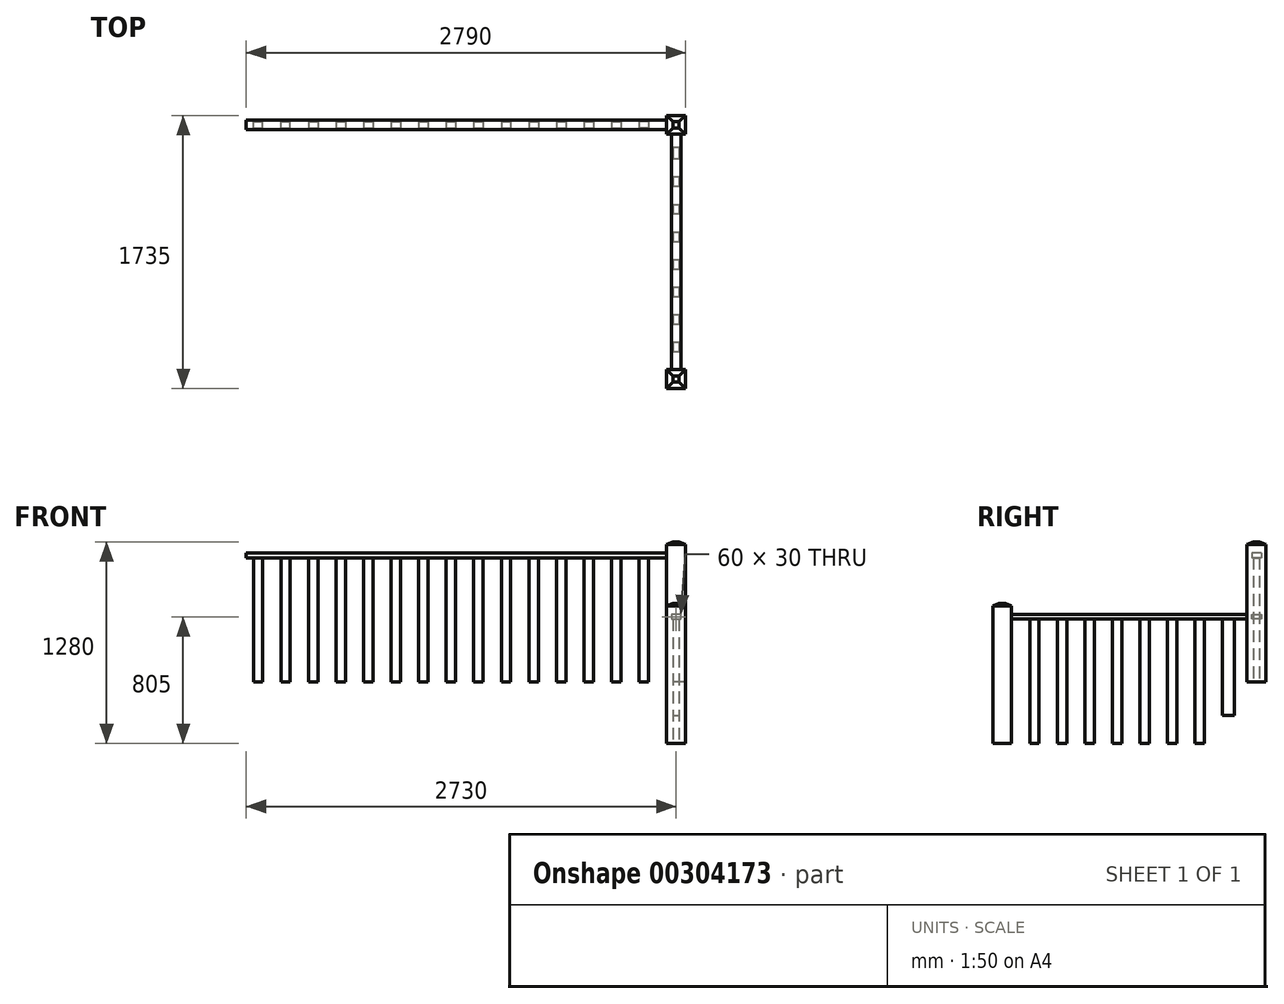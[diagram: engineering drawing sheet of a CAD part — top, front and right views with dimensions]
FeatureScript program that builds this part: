
annotation { "Feature Type Name" : "Feature", "Feature Type Description" : "" }
export const myFeature = defineFeature(function(context is Context, id is Id, definition is map)
    precondition{}
    {
        {
            var Q0;
            Q0=qCreatedBy(makeId("Top.planeOp"),FACE);
            var sketch = newSketch(context, id + "F0", { "sketchPlane" : qUnion([Q0])});
            skLineSegment(sketch, "E0.bottom", {"start": v(-80, 328.24) * mm, "end": v(40, 328.24) * mm});
            skLineSegment(sketch, "E0.top", {"start": v(-80, 208.24) * mm, "end": v(40, 208.24) * mm});
            skLineSegment(sketch, "E0.left", {"start": v(-80, 328.24) * mm, "end": v(-80, 208.24) * mm});
            skLineSegment(sketch, "E0.right", {"start": v(40, 328.24) * mm, "end": v(40, 208.24) * mm});
            skLineSegment(sketch, "E1.top", {"start": v(-80, 1823.24) * mm, "end": v(40, 1823.24) * mm});
            skLineSegment(sketch, "E1.left", {"start": v(-80, 1943.24) * mm, "end": v(-80, 1823.24) * mm});
            skLineSegment(sketch, "E1.right", {"start": v(40, 1943.24) * mm, "end": v(40, 1823.24) * mm});
            skLineSegment(sketch, "E2.bottom", {"start": v(-40, 503.24) * mm, "end": v(0, 503.24) * mm});
            skLineSegment(sketch, "E2.top", {"start": v(-40, 443.24) * mm, "end": v(0, 443.24) * mm});
            skLineSegment(sketch, "E2.left", {"start": v(-40, 503.24) * mm, "end": v(-40, 443.24) * mm});
            skLineSegment(sketch, "E2.right", {"start": v(0, 503.24) * mm, "end": v(0, 443.24) * mm});
            skLineSegment(sketch, "E3.bottom", {"start": v(-40, 678.24) * mm, "end": v(0, 678.24) * mm});
            skLineSegment(sketch, "E3.top", {"start": v(-40, 618.24) * mm, "end": v(0, 618.24) * mm});
            skLineSegment(sketch, "E3.left", {"start": v(-40, 678.24) * mm, "end": v(-40, 618.24) * mm});
            skLineSegment(sketch, "E3.right", {"start": v(0, 678.24) * mm, "end": v(0, 618.24) * mm});
            skLineSegment(sketch, "E4.bottom", {"start": v(-40, 853.24) * mm, "end": v(0, 853.24) * mm});
            skLineSegment(sketch, "E4.top", {"start": v(-40, 793.24) * mm, "end": v(0, 793.24) * mm});
            skLineSegment(sketch, "E4.left", {"start": v(-40, 853.24) * mm, "end": v(-40, 793.24) * mm});
            skLineSegment(sketch, "E4.right", {"start": v(0, 853.24) * mm, "end": v(0, 793.24) * mm});
            skLineSegment(sketch, "E5.bottom", {"start": v(-40, 1028.24) * mm, "end": v(0, 1028.24) * mm});
            skLineSegment(sketch, "E5.top", {"start": v(-40, 968.24) * mm, "end": v(0, 968.24) * mm});
            skLineSegment(sketch, "E5.left", {"start": v(-40, 1028.24) * mm, "end": v(-40, 968.24) * mm});
            skLineSegment(sketch, "E5.right", {"start": v(0, 1028.24) * mm, "end": v(0, 968.24) * mm});
            skLineSegment(sketch, "E6.bottom", {"start": v(-40, 1203.24) * mm, "end": v(0, 1203.24) * mm});
            skLineSegment(sketch, "E6.top", {"start": v(-40, 1143.24) * mm, "end": v(0, 1143.24) * mm});
            skLineSegment(sketch, "E6.left", {"start": v(-40, 1203.24) * mm, "end": v(-40, 1143.24) * mm});
            skLineSegment(sketch, "E6.right", {"start": v(0, 1203.24) * mm, "end": v(0, 1143.24) * mm});
            skLineSegment(sketch, "E7.bottom", {"start": v(-40, 1378.24) * mm, "end": v(0, 1378.24) * mm});
            skLineSegment(sketch, "E7.top", {"start": v(-40, 1318.24) * mm, "end": v(0, 1318.24) * mm});
            skLineSegment(sketch, "E7.left", {"start": v(-40, 1378.24) * mm, "end": v(-40, 1318.24) * mm});
            skLineSegment(sketch, "E7.right", {"start": v(0, 1378.24) * mm, "end": v(0, 1318.24) * mm});
            skLineSegment(sketch, "E8.bottom", {"start": v(-40, 1553.24) * mm, "end": v(0, 1553.24) * mm});
            skLineSegment(sketch, "E8.top", {"start": v(-40, 1493.24) * mm, "end": v(0, 1493.24) * mm});
            skLineSegment(sketch, "E8.left", {"start": v(-40, 1553.24) * mm, "end": v(-40, 1493.24) * mm});
            skLineSegment(sketch, "E8.right", {"start": v(0, 1553.24) * mm, "end": v(0, 1478.21) * mm});
            skLineSegment(sketch, "E9.bottom", {"start": v(-40, 1743.26) * mm, "end": v(0, 1743.26) * mm});
            skLineSegment(sketch, "E9.top", {"start": v(-40, 1668.24) * mm, "end": v(0, 1668.24) * mm});
            skLineSegment(sketch, "E9.left", {"start": v(-40, 1743.26) * mm, "end": v(-40, 1668.24) * mm});
            skLineSegment(sketch, "E9.right", {"start": v(0, 1743.26) * mm, "end": v(0, 1668.24) * mm});
            skLineSegment(sketch, "E10", {"start": v(40, 1943.24) * mm, "end": v(-80, 1943.24) * mm});
            skLineSegment(sketch, "E11.bottom", {"start": v(-195, 1903.24) * mm, "end": v(-255, 1903.24) * mm});
            skLineSegment(sketch, "E11.top", {"start": v(-195, 1863.24) * mm, "end": v(-255, 1863.24) * mm});
            skLineSegment(sketch, "E11.left", {"start": v(-195, 1903.24) * mm, "end": v(-195, 1863.24) * mm});
            skLineSegment(sketch, "E11.right", {"start": v(-255, 1903.24) * mm, "end": v(-255, 1863.24) * mm});
            skLineSegment(sketch, "E12.bottom", {"start": v(-370, 1903.24) * mm, "end": v(-430, 1903.24) * mm});
            skLineSegment(sketch, "E12.top", {"start": v(-370, 1863.24) * mm, "end": v(-430, 1863.24) * mm});
            skLineSegment(sketch, "E12.left", {"start": v(-370, 1903.24) * mm, "end": v(-370, 1863.24) * mm});
            skLineSegment(sketch, "E12.right", {"start": v(-430, 1903.24) * mm, "end": v(-430, 1863.24) * mm});
            skLineSegment(sketch, "E13.bottom", {"start": v(-545, 1903.24) * mm, "end": v(-605, 1903.24) * mm});
            skLineSegment(sketch, "E13.top", {"start": v(-545, 1863.24) * mm, "end": v(-605, 1863.24) * mm});
            skLineSegment(sketch, "E13.left", {"start": v(-545, 1903.24) * mm, "end": v(-545, 1863.24) * mm});
            skLineSegment(sketch, "E13.right", {"start": v(-605, 1903.24) * mm, "end": v(-605, 1863.24) * mm});
            skLineSegment(sketch, "E14.bottom", {"start": v(-720, 1903.24) * mm, "end": v(-780, 1903.24) * mm});
            skLineSegment(sketch, "E14.top", {"start": v(-720, 1863.24) * mm, "end": v(-780, 1863.24) * mm});
            skLineSegment(sketch, "E14.left", {"start": v(-720, 1903.24) * mm, "end": v(-720, 1863.24) * mm});
            skLineSegment(sketch, "E14.right", {"start": v(-780, 1903.24) * mm, "end": v(-780, 1863.24) * mm});
            skLineSegment(sketch, "E15.bottom", {"start": v(-895, 1903.24) * mm, "end": v(-955, 1903.24) * mm});
            skLineSegment(sketch, "E15.top", {"start": v(-895, 1863.24) * mm, "end": v(-955, 1863.24) * mm});
            skLineSegment(sketch, "E15.left", {"start": v(-895, 1903.24) * mm, "end": v(-895, 1863.24) * mm});
            skLineSegment(sketch, "E15.right", {"start": v(-955, 1903.24) * mm, "end": v(-955, 1863.24) * mm});
            skLineSegment(sketch, "E16.bottom", {"start": v(-1070, 1903.24) * mm, "end": v(-1130, 1903.24) * mm});
            skLineSegment(sketch, "E16.top", {"start": v(-1070, 1863.24) * mm, "end": v(-1130, 1863.24) * mm});
            skLineSegment(sketch, "E16.left", {"start": v(-1070, 1903.24) * mm, "end": v(-1070, 1863.24) * mm});
            skLineSegment(sketch, "E16.right", {"start": v(-1130, 1903.24) * mm, "end": v(-1130, 1863.24) * mm});
            skLineSegment(sketch, "E17.bottom", {"start": v(-1245, 1903.24) * mm, "end": v(-1305, 1903.24) * mm});
            skLineSegment(sketch, "E17.top", {"start": v(-1245, 1863.24) * mm, "end": v(-1305, 1863.24) * mm});
            skLineSegment(sketch, "E17.left", {"start": v(-1245, 1903.24) * mm, "end": v(-1245, 1863.24) * mm});
            skLineSegment(sketch, "E17.right", {"start": v(-1305, 1903.24) * mm, "end": v(-1305, 1863.24) * mm});
            skLineSegment(sketch, "E18.bottom", {"start": v(-1420, 1903.24) * mm, "end": v(-1480, 1903.24) * mm});
            skLineSegment(sketch, "E18.top", {"start": v(-1420, 1863.24) * mm, "end": v(-1480, 1863.24) * mm});
            skLineSegment(sketch, "E18.left", {"start": v(-1420, 1903.24) * mm, "end": v(-1420, 1863.24) * mm});
            skLineSegment(sketch, "E18.right", {"start": v(-1480, 1903.24) * mm, "end": v(-1480, 1863.24) * mm});
            skLineSegment(sketch, "E19.bottom", {"start": v(-1655, 1903.24) * mm, "end": v(-1595, 1903.24) * mm});
            skLineSegment(sketch, "E19.top", {"start": v(-1655, 1863.24) * mm, "end": v(-1595, 1863.24) * mm});
            skLineSegment(sketch, "E19.left", {"start": v(-1655, 1903.24) * mm, "end": v(-1655, 1863.24) * mm});
            skLineSegment(sketch, "E19.right", {"start": v(-1595, 1903.24) * mm, "end": v(-1595, 1863.24) * mm});
            skLineSegment(sketch, "E20.bottom", {"start": v(-1830, 1903.24) * mm, "end": v(-1770, 1903.24) * mm});
            skLineSegment(sketch, "E20.top", {"start": v(-1830, 1863.24) * mm, "end": v(-1770, 1863.24) * mm});
            skLineSegment(sketch, "E20.left", {"start": v(-1830, 1903.24) * mm, "end": v(-1830, 1863.24) * mm});
            skLineSegment(sketch, "E20.right", {"start": v(-1770, 1903.24) * mm, "end": v(-1770, 1863.24) * mm});
            skLineSegment(sketch, "E21.bottom", {"start": v(-2005, 1903.24) * mm, "end": v(-1945, 1903.24) * mm});
            skLineSegment(sketch, "E21.top", {"start": v(-2005, 1863.24) * mm, "end": v(-1945, 1863.24) * mm});
            skLineSegment(sketch, "E21.left", {"start": v(-2005, 1903.24) * mm, "end": v(-2005, 1863.24) * mm});
            skLineSegment(sketch, "E21.right", {"start": v(-1945, 1903.24) * mm, "end": v(-1945, 1863.24) * mm});
            skLineSegment(sketch, "E22.bottom", {"start": v(-2180, 1903.24) * mm, "end": v(-2120, 1903.24) * mm});
            skLineSegment(sketch, "E22.top", {"start": v(-2180, 1863.24) * mm, "end": v(-2120, 1863.24) * mm});
            skLineSegment(sketch, "E22.left", {"start": v(-2180, 1903.24) * mm, "end": v(-2180, 1863.24) * mm});
            skLineSegment(sketch, "E22.right", {"start": v(-2120, 1903.24) * mm, "end": v(-2120, 1863.24) * mm});
            skLineSegment(sketch, "E23.bottom", {"start": v(-2355, 1903.24) * mm, "end": v(-2295, 1903.24) * mm});
            skLineSegment(sketch, "E23.top", {"start": v(-2355, 1863.24) * mm, "end": v(-2295, 1863.24) * mm});
            skLineSegment(sketch, "E23.left", {"start": v(-2355, 1903.24) * mm, "end": v(-2355, 1863.24) * mm});
            skLineSegment(sketch, "E23.right", {"start": v(-2295, 1903.24) * mm, "end": v(-2295, 1863.24) * mm});
            skSolve(sketch);
        }
        {
            var Q0;
            Q0=makeQuery(id+"F0.imprint","IMPRINT",FACE,{"disambiguationData":[TD([[makeQuery(id+"F0.imprint","IMPRINT",EDGE,{"derivedFrom":sQuery(id+"F0.wireOp",EDGE,"E23.bottom")}),-1.0]])]});
            var Q1;
            Q1=makeQuery(id+"F0.imprint","IMPRINT",FACE,{"disambiguationData":[TD([[makeQuery(id+"F0.imprint","IMPRINT",EDGE,{"derivedFrom":sQuery(id+"F0.wireOp",EDGE,"E22.bottom")}),-1.0]])]});
            var Q2;
            Q2=makeQuery(id+"F0.imprint","IMPRINT",FACE,{"disambiguationData":[TD([[makeQuery(id+"F0.imprint","IMPRINT",EDGE,{"derivedFrom":sQuery(id+"F0.wireOp",EDGE,"E21.bottom")}),-1.0]])]});
            var Q3;
            Q3=makeQuery(id+"F0.imprint","IMPRINT",FACE,{"disambiguationData":[TD([[makeQuery(id+"F0.imprint","IMPRINT",EDGE,{"derivedFrom":sQuery(id+"F0.wireOp",EDGE,"E20.bottom")}),-1.0]])]});
            var Q4;
            Q4=makeQuery(id+"F0.imprint","IMPRINT",FACE,{"disambiguationData":[TD([[makeQuery(id+"F0.imprint","IMPRINT",EDGE,{"derivedFrom":sQuery(id+"F0.wireOp",EDGE,"E19.bottom")}),-1.0]])]});
            var Q5;
            Q5=makeQuery(id+"F0.imprint","IMPRINT",FACE,{"disambiguationData":[TD([[makeQuery(id+"F0.imprint","IMPRINT",EDGE,{"derivedFrom":sQuery(id+"F0.wireOp",EDGE,"E18.bottom")}),1.0]])]});
            var Q6;
            Q6=makeQuery(id+"F0.imprint","IMPRINT",FACE,{"disambiguationData":[TD([[makeQuery(id+"F0.imprint","IMPRINT",EDGE,{"derivedFrom":sQuery(id+"F0.wireOp",EDGE,"E17.bottom")}),1.0]])]});
            var Q7;
            Q7=makeQuery(id+"F0.imprint","IMPRINT",FACE,{"disambiguationData":[TD([[makeQuery(id+"F0.imprint","IMPRINT",EDGE,{"derivedFrom":sQuery(id+"F0.wireOp",EDGE,"E16.bottom")}),1.0]])]});
            var Q8;
            Q8=makeQuery(id+"F0.imprint","IMPRINT",FACE,{"disambiguationData":[TD([[makeQuery(id+"F0.imprint","IMPRINT",EDGE,{"derivedFrom":sQuery(id+"F0.wireOp",EDGE,"E15.bottom")}),1.0]])]});
            var Q9;
            Q9=makeQuery(id+"F0.imprint","IMPRINT",FACE,{"disambiguationData":[TD([[makeQuery(id+"F0.imprint","IMPRINT",EDGE,{"derivedFrom":sQuery(id+"F0.wireOp",EDGE,"E14.bottom")}),1.0]])]});
            var Q10;
            Q10=makeQuery(id+"F0.imprint","IMPRINT",FACE,{"disambiguationData":[TD([[makeQuery(id+"F0.imprint","IMPRINT",EDGE,{"derivedFrom":sQuery(id+"F0.wireOp",EDGE,"E13.bottom")}),1.0]])]});
            var Q11;
            Q11=makeQuery(id+"F0.imprint","IMPRINT",FACE,{"disambiguationData":[TD([[makeQuery(id+"F0.imprint","IMPRINT",EDGE,{"derivedFrom":sQuery(id+"F0.wireOp",EDGE,"E12.bottom")}),1.0]])]});
            var Q12;
            Q12=makeQuery(id+"F0.imprint","IMPRINT",FACE,{"disambiguationData":[TD([[makeQuery(id+"F0.imprint","IMPRINT",EDGE,{"derivedFrom":sQuery(id+"F0.wireOp",EDGE,"E11.bottom")}),1.0]])]});
            var Q13;
            Q13=makeQuery(id+"F0.imprint","IMPRINT",FACE,{"disambiguationData":[TD([[makeQuery(id+"F0.imprint","IMPRINT",EDGE,{"derivedFrom":sQuery(id+"F0.wireOp",EDGE,"E9.bottom")}),-1.0]])]});
            var Q14;
            {var subQ0=sQuery(id+"F0.wireOp",EDGE,"E8.bottom");Q14=makeQuery(id+"F0.imprint","IMPRINT",FACE,{"disambiguationData":[TD([[makeQuery(id+"F0.imprint","IMPRINT",EDGE,{"derivedFrom":subQ0}),-1.0]])]});}
            var Q15;
            Q15=makeQuery(id+"F0.imprint","IMPRINT",FACE,{"disambiguationData":[TD([[makeQuery(id+"F0.imprint","IMPRINT",EDGE,{"derivedFrom":sQuery(id+"F0.wireOp",EDGE,"E7.bottom")}),-1.0]])]});
            var Q16;
            Q16=makeQuery(id+"F0.imprint","IMPRINT",FACE,{"disambiguationData":[TD([[makeQuery(id+"F0.imprint","IMPRINT",EDGE,{"derivedFrom":sQuery(id+"F0.wireOp",EDGE,"E6.bottom")}),-1.0]])]});
            var Q17;
            Q17=makeQuery(id+"F0.imprint","IMPRINT",FACE,{"disambiguationData":[TD([[makeQuery(id+"F0.imprint","IMPRINT",EDGE,{"derivedFrom":sQuery(id+"F0.wireOp",EDGE,"E5.bottom")}),-1.0]])]});
            var Q18;
            Q18=makeQuery(id+"F0.imprint","IMPRINT",FACE,{"disambiguationData":[TD([[makeQuery(id+"F0.imprint","IMPRINT",EDGE,{"derivedFrom":sQuery(id+"F0.wireOp",EDGE,"E4.bottom")}),-1.0]])]});
            var Q19;
            Q19=makeQuery(id+"F0.imprint","IMPRINT",FACE,{"disambiguationData":[TD([[makeQuery(id+"F0.imprint","IMPRINT",EDGE,{"derivedFrom":sQuery(id+"F0.wireOp",EDGE,"E3.bottom")}),-1.0]])]});
            var Q20;
            Q20=makeQuery(id+"F0.imprint","IMPRINT",FACE,{"disambiguationData":[TD([[makeQuery(id+"F0.imprint","IMPRINT",EDGE,{"derivedFrom":sQuery(id+"F0.wireOp",EDGE,"E2.bottom")}),-1.0]])]});
            var Q21;
            Q21=makeQuery(id+"F0.imprint","IMPRINT",FACE,{"disambiguationData":[TD([[makeQuery(id+"F0.imprint","IMPRINT",EDGE,{"derivedFrom":sQuery(id+"F0.wireOp",EDGE,"E1.top")}),1.0]])]});
            var Q22;
            Q22=makeQuery(id+"F0.imprint","IMPRINT",FACE,{"disambiguationData":[TD([[makeQuery(id+"F0.imprint","IMPRINT",EDGE,{"derivedFrom":sQuery(id+"F0.wireOp",EDGE,"E0.bottom")}),-1.0]])]});
            extrude(context, id + "F1", {"entities" : qUnion([Q0, Q1, Q2, Q3, Q4, Q5, Q6, Q7, Q8, Q9, Q10, Q11, Q12, Q13, Q14, Q15, Q16, Q17, Q18, Q19, Q20, Q21, Q22]), "depth" : 790 * mm});
        }
        {
            var Q0;
            Q0=makeQuery(id+"F1.opExtrude","CAP_FACE",FACE,{"disambiguationData":[OSD([sQuery(id+"F0.wireOp",EDGE,"E9.bottom"),sQuery(id+"F0.wireOp",EDGE,"E9.top"),sQuery(id+"F0.wireOp",EDGE,"E9.left"),sQuery(id+"F0.wireOp",EDGE,"E9.right")])],"isStart":false});
            var sketch = newSketch(context, id + "F2", { "sketchPlane" : qUnion([Q0])});
            skPoint(sketch, "E24.0", {"position": v(-20, 328.24) * mm});
            skLineSegment(sketch, "E25.0", {"start": v(-80, 328.24) * mm, "end": v(40, 328.24) * mm});
            skLineSegment(sketch, "E26.0.0", {"start": v(-80, 328.24) * mm, "end": v(-80, 208.24) * mm});
            skLineSegment(sketch, "E26.0.1", {"start": v(-80, 208.24) * mm, "end": v(40, 208.24) * mm});
            skLineSegment(sketch, "E26.0.2", {"start": v(40, 208.24) * mm, "end": v(40, 328.24) * mm});
            skLineSegment(sketch, "E26.0.3", {"start": v(40, 328.24) * mm, "end": v(-80, 328.24) * mm});
            skLineSegment(sketch, "E27", {"start": v(-50, 1853.24) * mm, "end": v(-2417.72, 1853.24) * mm});
            skLineSegment(sketch, "E28", {"start": v(-2417.72, 1853.24) * mm, "end": v(-2417.72, 1913.24) * mm});
            skLineSegment(sketch, "E29", {"start": v(-2417.72, 1913.24) * mm, "end": v(10, 1913.24) * mm});
            skLineSegment(sketch, "E30", {"start": v(10, 1913.24) * mm, "end": v(10, 328.24) * mm});
            skLineSegment(sketch, "E31", {"start": v(10, 328.24) * mm, "end": v(-50, 328.24) * mm});
            skLineSegment(sketch, "E32", {"start": v(-50, 328.24) * mm, "end": v(-50, 1853.24) * mm});
            skSolve(sketch);
        }
        {
            var Q0;
            Q0 = qSketchRegion(id + "F2", true);
            extrude(context, id + "F3", {"entities" : qUnion([Q0]), "depth" : 30 * mm});
        }
        {
            var Q0;
            Q0=makeQuery(id+"F1.opExtrude","CAP_FACE",FACE,{"disambiguationData":[OSD([sQuery(id+"F0.wireOp",EDGE,"E1.top"),sQuery(id+"F0.wireOp",EDGE,"E1.left"),sQuery(id+"F0.wireOp",EDGE,"E1.right"),sQuery(id+"F0.wireOp",EDGE,"E10")])],"isStart":false});
            var sketch = newSketch(context, id + "F4", { "sketchPlane" : qUnion([Q0])});
            skLineSegment(sketch, "E33.0", {"start": v(40, 1943.24) * mm, "end": v(-80, 1943.24) * mm});
            skLineSegment(sketch, "E34.0", {"start": v(-80, 1943.24) * mm, "end": v(-80, 1823.24) * mm});
            skLineSegment(sketch, "E35.0", {"start": v(-80, 1823.24) * mm, "end": v(40, 1823.24) * mm});
            skLineSegment(sketch, "E36.0", {"start": v(40, 1943.24) * mm, "end": v(40, 1823.24) * mm});
            skLineSegment(sketch, "E37.0", {"start": v(-80, 328.24) * mm, "end": v(-80, 208.24) * mm});
            skPoint(sketch, "E38.0", {"position": v(40, 208.24) * mm});
            skLineSegment(sketch, "E39.bottom", {"start": v(-80, 328.24) * mm, "end": v(40, 328.24) * mm});
            skLineSegment(sketch, "E39.top", {"start": v(-80, 208.24) * mm, "end": v(40, 208.24) * mm});
            skLineSegment(sketch, "E39.right", {"start": v(40, 328.24) * mm, "end": v(40, 208.24) * mm});
            skLineSegment(sketch, "E40.bottom", {"start": v(-80, 1943.24) * mm, "end": v(40, 1943.24) * mm});
            skSolve(sketch);
        }
        {
            var Q0;
            Q0 = qSketchRegion(id + "F4", true);
            extrude(context, id + "F5", {"entities" : qUnion([Q0]), "depth" : 100 * mm});
        }
        {
            var Q0;
            Q0=makeQuery(id+"F5.opExtrude","CAP_EDGE",EDGE,{"disambiguationData":[OSD([sQuery(id+"F4.wireOp",EDGE,"E39.right")])],"isStart":false});
            var Q1;
            Q1=makeQuery(id+"F5.opExtrude","CAP_EDGE",EDGE,{"disambiguationData":[OSD([sQuery(id+"F4.wireOp",EDGE,"E39.top")])],"isStart":false});
            var Q2;
            Q2=makeQuery(id+"F5.opExtrude","CAP_EDGE",EDGE,{"disambiguationData":[OSD([sQuery(id+"F4.wireOp",EDGE,"E37.0")])],"isStart":false});
            var Q3;
            Q3=makeQuery(id+"F5.opExtrude","CAP_EDGE",EDGE,{"disambiguationData":[OSD([sQuery(id+"F4.wireOp",EDGE,"E39.bottom")])],"isStart":false});
            chamfer(context, id + "F6", {"entities" : qUnion([Q0, Q1, Q2, Q3]), "chamferType" : ChamferType.TWO_OFFSETS, "width1" : 15 * mm, "oppositeDirection" : false, "width2" : 40 * mm, "tangentPropagation" : true});
        }
        {
            var Q0;
            Q0=makeQuery(id+"F1.opExtrude","SWEPT_BODY",BODY,{"disambiguationData":[OSD([sQuery(id+"F0.wireOp",EDGE,"E0.bottom"),sQuery(id+"F0.wireOp",EDGE,"E0.top"),sQuery(id+"F0.wireOp",EDGE,"E0.left"),sQuery(id+"F0.wireOp",EDGE,"E0.right")])]});
            var Q1;
            Q1=makeQuery(id+"F1.opExtrude","SWEPT_BODY",BODY,{"disambiguationData":[OSD([sQuery(id+"F0.wireOp",EDGE,"E1.top"),sQuery(id+"F0.wireOp",EDGE,"E1.left"),sQuery(id+"F0.wireOp",EDGE,"E1.right"),sQuery(id+"F0.wireOp",EDGE,"E10")])]});
            var Q2;
            Q2=makeQuery(id+"F1.opExtrude","SWEPT_BODY",BODY,{"disambiguationData":[OSD([sQuery(id+"F0.wireOp",EDGE,"E2.bottom"),sQuery(id+"F0.wireOp",EDGE,"E2.top"),sQuery(id+"F0.wireOp",EDGE,"E2.left"),sQuery(id+"F0.wireOp",EDGE,"E2.right")])]});
            var Q3;
            Q3=makeQuery(id+"F1.opExtrude","SWEPT_BODY",BODY,{"disambiguationData":[OSD([sQuery(id+"F0.wireOp",EDGE,"E3.bottom"),sQuery(id+"F0.wireOp",EDGE,"E3.top"),sQuery(id+"F0.wireOp",EDGE,"E3.left"),sQuery(id+"F0.wireOp",EDGE,"E3.right")])]});
            var Q4;
            Q4=makeQuery(id+"F1.opExtrude","SWEPT_BODY",BODY,{"disambiguationData":[OSD([sQuery(id+"F0.wireOp",EDGE,"E4.bottom"),sQuery(id+"F0.wireOp",EDGE,"E4.top"),sQuery(id+"F0.wireOp",EDGE,"E4.left"),sQuery(id+"F0.wireOp",EDGE,"E4.right")])]});
            var Q5;
            Q5=makeQuery(id+"F1.opExtrude","SWEPT_BODY",BODY,{"disambiguationData":[OSD([sQuery(id+"F0.wireOp",EDGE,"E5.bottom"),sQuery(id+"F0.wireOp",EDGE,"E5.top"),sQuery(id+"F0.wireOp",EDGE,"E5.left"),sQuery(id+"F0.wireOp",EDGE,"E5.right")])]});
            var Q6;
            Q6=makeQuery(id+"F1.opExtrude","SWEPT_BODY",BODY,{"disambiguationData":[OSD([sQuery(id+"F0.wireOp",EDGE,"E6.bottom"),sQuery(id+"F0.wireOp",EDGE,"E6.top"),sQuery(id+"F0.wireOp",EDGE,"E6.left"),sQuery(id+"F0.wireOp",EDGE,"E6.right")])]});
            var Q7;
            Q7=makeQuery(id+"F1.opExtrude","SWEPT_BODY",BODY,{"disambiguationData":[OSD([sQuery(id+"F0.wireOp",EDGE,"E7.bottom"),sQuery(id+"F0.wireOp",EDGE,"E7.top"),sQuery(id+"F0.wireOp",EDGE,"E7.left"),sQuery(id+"F0.wireOp",EDGE,"E7.right")])]});
            var Q8;
            Q8=makeQuery(id+"F1.opExtrude","SWEPT_BODY",BODY,{"disambiguationData":[OSD([sQuery(id+"F0.wireOp",EDGE,"E8.bottom"),sQuery(id+"F0.wireOp",EDGE,"E8.top"),sQuery(id+"F0.wireOp",EDGE,"E8.left"),sQuery(id+"F0.wireOp",EDGE,"E8.right")])]});
            var Q9;
            Q9=makeQuery(id+"F1.opExtrude","SWEPT_BODY",BODY,{"disambiguationData":[OSD([sQuery(id+"F0.wireOp",EDGE,"E9.bottom"),sQuery(id+"F0.wireOp",EDGE,"E9.top"),sQuery(id+"F0.wireOp",EDGE,"E9.left"),sQuery(id+"F0.wireOp",EDGE,"E9.right")])]});
            var Q10;
            Q10=makeQuery(id+"F1.opExtrude","SWEPT_BODY",BODY,{"disambiguationData":[OSD([sQuery(id+"F0.wireOp",EDGE,"E11.bottom"),sQuery(id+"F0.wireOp",EDGE,"E11.top"),sQuery(id+"F0.wireOp",EDGE,"E11.left"),sQuery(id+"F0.wireOp",EDGE,"E11.right")])]});
            var Q11;
            Q11=makeQuery(id+"F1.opExtrude","SWEPT_BODY",BODY,{"disambiguationData":[OSD([sQuery(id+"F0.wireOp",EDGE,"E12.bottom"),sQuery(id+"F0.wireOp",EDGE,"E12.top"),sQuery(id+"F0.wireOp",EDGE,"E12.left"),sQuery(id+"F0.wireOp",EDGE,"E12.right")])]});
            var Q12;
            Q12=makeQuery(id+"F1.opExtrude","SWEPT_BODY",BODY,{"disambiguationData":[OSD([sQuery(id+"F0.wireOp",EDGE,"E13.bottom"),sQuery(id+"F0.wireOp",EDGE,"E13.top"),sQuery(id+"F0.wireOp",EDGE,"E13.left"),sQuery(id+"F0.wireOp",EDGE,"E13.right")])]});
            var Q13;
            Q13=makeQuery(id+"F1.opExtrude","SWEPT_BODY",BODY,{"disambiguationData":[OSD([sQuery(id+"F0.wireOp",EDGE,"E14.bottom"),sQuery(id+"F0.wireOp",EDGE,"E14.top"),sQuery(id+"F0.wireOp",EDGE,"E14.left"),sQuery(id+"F0.wireOp",EDGE,"E14.right")])]});
            var Q14;
            Q14=makeQuery(id+"F1.opExtrude","SWEPT_BODY",BODY,{"disambiguationData":[OSD([sQuery(id+"F0.wireOp",EDGE,"E15.bottom"),sQuery(id+"F0.wireOp",EDGE,"E15.top"),sQuery(id+"F0.wireOp",EDGE,"E15.left"),sQuery(id+"F0.wireOp",EDGE,"E15.right")])]});
            var Q15;
            Q15=makeQuery(id+"F1.opExtrude","SWEPT_BODY",BODY,{"disambiguationData":[OSD([sQuery(id+"F0.wireOp",EDGE,"E16.bottom"),sQuery(id+"F0.wireOp",EDGE,"E16.top"),sQuery(id+"F0.wireOp",EDGE,"E16.left"),sQuery(id+"F0.wireOp",EDGE,"E16.right")])]});
            var Q16;
            Q16=makeQuery(id+"F1.opExtrude","SWEPT_BODY",BODY,{"disambiguationData":[OSD([sQuery(id+"F0.wireOp",EDGE,"E17.bottom"),sQuery(id+"F0.wireOp",EDGE,"E17.top"),sQuery(id+"F0.wireOp",EDGE,"E17.left"),sQuery(id+"F0.wireOp",EDGE,"E17.right")])]});
            var Q17;
            Q17=makeQuery(id+"F1.opExtrude","SWEPT_BODY",BODY,{"disambiguationData":[OSD([sQuery(id+"F0.wireOp",EDGE,"E18.bottom"),sQuery(id+"F0.wireOp",EDGE,"E18.top"),sQuery(id+"F0.wireOp",EDGE,"E18.left"),sQuery(id+"F0.wireOp",EDGE,"E18.right")])]});
            var Q18;
            Q18=makeQuery(id+"F1.opExtrude","SWEPT_BODY",BODY,{"disambiguationData":[OSD([sQuery(id+"F0.wireOp",EDGE,"E19.bottom"),sQuery(id+"F0.wireOp",EDGE,"E19.top"),sQuery(id+"F0.wireOp",EDGE,"E19.left"),sQuery(id+"F0.wireOp",EDGE,"E19.right")])]});
            var Q19;
            Q19=makeQuery(id+"F1.opExtrude","SWEPT_BODY",BODY,{"disambiguationData":[OSD([sQuery(id+"F0.wireOp",EDGE,"E20.bottom"),sQuery(id+"F0.wireOp",EDGE,"E20.top"),sQuery(id+"F0.wireOp",EDGE,"E20.left"),sQuery(id+"F0.wireOp",EDGE,"E20.right")])]});
            var Q20;
            Q20=makeQuery(id+"F1.opExtrude","SWEPT_BODY",BODY,{"disambiguationData":[OSD([sQuery(id+"F0.wireOp",EDGE,"E21.bottom"),sQuery(id+"F0.wireOp",EDGE,"E21.top"),sQuery(id+"F0.wireOp",EDGE,"E21.left"),sQuery(id+"F0.wireOp",EDGE,"E21.right")])]});
            var Q21;
            Q21=makeQuery(id+"F1.opExtrude","SWEPT_BODY",BODY,{"disambiguationData":[OSD([sQuery(id+"F0.wireOp",EDGE,"E22.bottom"),sQuery(id+"F0.wireOp",EDGE,"E22.top"),sQuery(id+"F0.wireOp",EDGE,"E22.left"),sQuery(id+"F0.wireOp",EDGE,"E22.right")])]});
            var Q22;
            Q22=makeQuery(id+"F1.opExtrude","SWEPT_BODY",BODY,{"disambiguationData":[OSD([sQuery(id+"F0.wireOp",EDGE,"E23.bottom"),sQuery(id+"F0.wireOp",EDGE,"E23.top"),sQuery(id+"F0.wireOp",EDGE,"E23.left"),sQuery(id+"F0.wireOp",EDGE,"E23.right")])]});
            var Q23;
            Q23=makeQuery(id+"F3.opExtrude","SWEPT_BODY",BODY,{"disambiguationData":[OSD([sQuery(id+"F2.wireOp",EDGE,"E26.0.0"),sQuery(id+"F2.wireOp",EDGE,"E26.0.1"),sQuery(id+"F2.wireOp",EDGE,"E26.0.2"),sQuery(id+"F2.wireOp",EDGE,"E26.0.3"),sQuery(id+"F2.wireOp",EDGE,"E27"),sQuery(id+"F2.wireOp",EDGE,"E28"),sQuery(id+"F2.wireOp",EDGE,"E29"),sQuery(id+"F2.wireOp",EDGE,"E30"),sQuery(id+"F2.wireOp",EDGE,"E32")])]});
            var Q24;
            Q24=makeQuery(id+"F5.opExtrude","SWEPT_BODY",BODY,{"disambiguationData":[OSD([sQuery(id+"F4.wireOp",EDGE,"E39.bottom"),sQuery(id+"F4.wireOp",EDGE,"E39.top"),sQuery(id+"F4.wireOp",EDGE,"E37.0"),sQuery(id+"F4.wireOp",EDGE,"E39.right")])]});
            var Q25;
            Q25=makeQuery(id+"F5.opExtrude","SWEPT_BODY",BODY,{"disambiguationData":[OSD([sQuery(id+"F4.wireOp",EDGE,"E40.bottom"),sQuery(id+"F4.wireOp",EDGE,"E35.0"),sQuery(id+"F4.wireOp",EDGE,"E34.0"),sQuery(id+"F4.wireOp",EDGE,"E36.0")])]});
            booleanBodies(context, id + "F7", {"operationType" : BooleanOperationType.UNION, "tools" : qUnion([Q0, Q1, Q2, Q3, Q4, Q5, Q6, Q7, Q8, Q9, Q10, Q11, Q12, Q13, Q14, Q15, Q16, Q17, Q18, Q19, Q20, Q21, Q22, Q23, Q24, Q25])});
        }
        {
            var Q0;
            Q0=makeQuery(id+"F1.opExtrude","CAP_FACE",FACE,{"disambiguationData":[OSD([sQuery(id+"F0.wireOp",EDGE,"E23.bottom"),sQuery(id+"F0.wireOp",EDGE,"E23.top"),sQuery(id+"F0.wireOp",EDGE,"E23.left"),sQuery(id+"F0.wireOp",EDGE,"E23.right")])],"isStart":true});
            var sketch = newSketch(context, id + "F8", { "sketchPlane" : qUnion([Q0])});
            skLineSegment(sketch, "E41.top", {"start": v(-2551.9, -1788.92) * mm, "end": v(302.39, -1788.92) * mm});
            skLineSegment(sketch, "E41.left", {"start": v(-2551.9, -1948.92) * mm, "end": v(-2551.9, -1788.92) * mm});
            skLineSegment(sketch, "E41.right", {"start": v(302.39, -1948.92) * mm, "end": v(302.39, -1788.92) * mm});
            skLineSegment(sketch, "E42", {"start": v(-2551.9, -1948.92) * mm, "end": v(302.39, -1948.92) * mm});
            skSolve(sketch);
        }
        {
            var Q0;
            Q0=makeQuery(id+"F8.imprint","IMPRINT",FACE,{"disambiguationData":[TD([[makeQuery(id+"F8.imprint","IMPRINT",EDGE,{"derivedFrom":sQuery(id+"F8.wireOp",EDGE,"E41.top")}),-1.0]])]});
            var Q1;
            Q1=makeQuery(id+"F8.imprint","IMPRINT",FACE,{"disambiguationData":[TD([[makeQuery(id+"F8.imprint","IMPRINT",EDGE,{"derivedFrom":makeQuery(id+"F1.opExtrude","CAP_EDGE",EDGE,{"disambiguationData":[OSD([sQuery(id+"F0.wireOp",EDGE,"E23.bottom")])],"isStart":true})}),1.0]])]});
            extrude(context, id + "F9", {"entities" : qUnion([Q0, Q1]), "operationType" : NewBodyOperationType.REMOVE, "oppositeDirection" : true, "depth" : 390 * mm});
        }
        {
            var Q0;
            Q0=makeQuery(id+"F1.opExtrude","CAP_FACE",FACE,{"disambiguationData":[OSD([sQuery(id+"F0.wireOp",EDGE,"E9.bottom"),sQuery(id+"F0.wireOp",EDGE,"E9.top"),sQuery(id+"F0.wireOp",EDGE,"E9.left"),sQuery(id+"F0.wireOp",EDGE,"E9.right")])],"isStart":true});
            var sketch = newSketch(context, id + "F10", { "sketchPlane" : qUnion([Q0])});
            skSolve(sketch);
        }
        {
            var Q0;
            Q0=makeQuery(id+"F10.imprint","IMPRINT",FACE,{"disambiguationData":[TD([[makeQuery(id+"F10.imprint","IMPRINT",EDGE,{"derivedFrom":makeQuery(id+"F1.opExtrude","CAP_EDGE",EDGE,{"disambiguationData":[OSD([sQuery(id+"F0.wireOp",EDGE,"E9.bottom")])],"isStart":true})}),1.0]])]});
            extrude(context, id + "F11", {"entities" : qUnion([Q0]), "operationType" : NewBodyOperationType.REMOVE, "oppositeDirection" : true, "depth" : 180 * mm});
        }
        {
            var Q0;
            Q0=makeQuery(id+"F5.opExtrude","CAP_FACE",FACE,{"disambiguationData":[OSD([sQuery(id+"F4.wireOp",EDGE,"E40.bottom"),sQuery(id+"F4.wireOp",EDGE,"E35.0"),sQuery(id+"F4.wireOp",EDGE,"E34.0"),sQuery(id+"F4.wireOp",EDGE,"E36.0")])],"isStart":false});
            var sketch = newSketch(context, id + "F12", { "sketchPlane" : qUnion([Q0])});
            skPoint(sketch, "E43.0", {"position": v(-80, 1943.24) * mm});
            skPoint(sketch, "E44.0", {"position": v(40, 1823.24) * mm});
            skLineSegment(sketch, "E45.bottom", {"start": v(-80, 1943.24) * mm, "end": v(40, 1943.24) * mm});
            skLineSegment(sketch, "E45.top", {"start": v(-80, 1823.24) * mm, "end": v(40, 1823.24) * mm});
            skLineSegment(sketch, "E45.left", {"start": v(-80, 1943.24) * mm, "end": v(-80, 1823.24) * mm});
            skLineSegment(sketch, "E45.right", {"start": v(40, 1943.24) * mm, "end": v(40, 1823.24) * mm});
            skSolve(sketch);
        }
        {
            var Q0;
            Q0=makeQuery(id+"F12.imprint","IMPRINT",FACE,{"disambiguationData":[TD([[makeQuery(id+"F12.imprint","IMPRINT",EDGE,{"derivedFrom":sQuery(id+"F12.wireOp",EDGE,"E45.bottom")}),1.0]])]});
            extrude(context, id + "F13", {"entities" : qUnion([Q0]), "operationType" : NewBodyOperationType.ADD, "depth" : 390 * mm});
        }
        {
            var Q0;
            Q0=makeQuery(id+"F13.opExtrude","CAP_EDGE",EDGE,{"disambiguationData":[OSD([sQuery(id+"F12.wireOp",EDGE,"E45.top")])],"isStart":false});
            var Q1;
            Q1=makeQuery(id+"F13.opExtrude","CAP_EDGE",EDGE,{"disambiguationData":[OSD([sQuery(id+"F12.wireOp",EDGE,"E45.left")])],"isStart":false});
            var Q2;
            Q2=makeQuery(id+"F13.opExtrude","CAP_EDGE",EDGE,{"disambiguationData":[OSD([sQuery(id+"F12.wireOp",EDGE,"E45.bottom")])],"isStart":false});
            var Q3;
            Q3=makeQuery(id+"F13.opExtrude","CAP_EDGE",EDGE,{"disambiguationData":[OSD([sQuery(id+"F12.wireOp",EDGE,"E45.right")])],"isStart":false});
            chamfer(context, id + "F14", {"entities" : qUnion([Q0, Q1, Q2, Q3]), "chamferType" : ChamferType.TWO_OFFSETS, "width1" : 40 * mm, "oppositeDirection" : false, "width2" : 15 * mm, "tangentPropagation" : true});
        }
        {
            var Q0;
            Q0=makeQuery(id+"F3.opExtrude","SWEPT_FACE",FACE,{"disambiguationData":[OSD([sQuery(id+"F2.wireOp",EDGE,"E28")])]});
            var sketch = newSketch(context, id + "F15", { "sketchPlane" : qUnion([Q0])});
            skPoint(sketch, "E46.0", {"position": v(-1913.24, 790) * mm});
            skPoint(sketch, "E47.0", {"position": v(-1853.24, 820) * mm});
            skLineSegment(sketch, "E48.bottom", {"start": v(-1913.24, 790) * mm, "end": v(-1853.24, 790) * mm});
            skLineSegment(sketch, "E48.top", {"start": v(-1913.24, 820) * mm, "end": v(-1853.24, 820) * mm});
            skLineSegment(sketch, "E48.left", {"start": v(-1913.24, 790) * mm, "end": v(-1913.24, 820) * mm});
            skLineSegment(sketch, "E48.right", {"start": v(-1853.24, 790) * mm, "end": v(-1853.24, 820) * mm});
            skSolve(sketch);
        }
        {
            var Q0;
            Q0=makeQuery(id+"F15.imprint","IMPRINT",FACE,{"disambiguationData":[TD([[makeQuery(id+"F15.imprint","IMPRINT",EDGE,{"derivedFrom":sQuery(id+"F15.wireOp",EDGE,"E48.bottom")}),-1.0]])]});
            extrude(context, id + "F16", {"entities" : qUnion([Q0]), "operationType" : NewBodyOperationType.REMOVE, "oppositeDirection" : true, "depth" : 2337.74 * mm});
        }
        {
            var Q0;
            Q0=makeQuery(id+"F16.boolean.opBoolean","COPY",FACE,{"disambiguationData":[TD([makeQuery(id+"F1.opExtrude","SWEPT_FACE",FACE,{"disambiguationData":[OSD([sQuery(id+"F0.wireOp",EDGE,"E11.bottom")])]})])],"derivedFrom":makeQuery(id+"F16.opExtrude","SWEPT_FACE",FACE,{"disambiguationData":[OSD([sQuery(id+"F15.wireOp",EDGE,"E48.bottom")])]})});
            var sketch = newSketch(context, id + "F17", { "sketchPlane" : qUnion([Q0])});
            skPoint(sketch, "E49.0", {"position": v(-2355, 1903.24) * mm});
            skPoint(sketch, "E50.0", {"position": v(-2295, 1863.24) * mm});
            skPoint(sketch, "E51.0", {"position": v(-2180, 1903.24) * mm});
            skPoint(sketch, "E52.0", {"position": v(-2120, 1863.24) * mm});
            skPoint(sketch, "E53.0", {"position": v(-2005, 1903.24) * mm});
            skPoint(sketch, "E54.0", {"position": v(-1945, 1863.24) * mm});
            skPoint(sketch, "E55.0", {"position": v(-1830, 1903.24) * mm});
            skPoint(sketch, "E56.0", {"position": v(-1770, 1863.24) * mm});
            skPoint(sketch, "E57.0", {"position": v(-1655, 1903.24) * mm});
            skPoint(sketch, "E58.0", {"position": v(-1595, 1863.24) * mm});
            skPoint(sketch, "E59.0", {"position": v(-1480, 1903.24) * mm});
            skPoint(sketch, "E60.0", {"position": v(-1420, 1863.24) * mm});
            skPoint(sketch, "E61.0", {"position": v(-1305, 1903.24) * mm});
            skPoint(sketch, "E62.0", {"position": v(-1245, 1863.24) * mm});
            skPoint(sketch, "E63.0", {"position": v(-1130, 1903.24) * mm});
            skPoint(sketch, "E64.0", {"position": v(-1070, 1863.24) * mm});
            skPoint(sketch, "E65.0", {"position": v(-955, 1903.24) * mm});
            skPoint(sketch, "E66.0", {"position": v(-895, 1863.24) * mm});
            skPoint(sketch, "E67.0", {"position": v(-780, 1903.24) * mm});
            skPoint(sketch, "E68.0", {"position": v(-720, 1863.24) * mm});
            skPoint(sketch, "E69.0", {"position": v(-605, 1903.24) * mm});
            skPoint(sketch, "E70.0", {"position": v(-545, 1863.24) * mm});
            skPoint(sketch, "E71.0", {"position": v(-430, 1903.24) * mm});
            skPoint(sketch, "E72.0", {"position": v(-370, 1863.24) * mm});
            skPoint(sketch, "E73.0", {"position": v(-255, 1903.24) * mm});
            skPoint(sketch, "E74.0", {"position": v(-195, 1863.24) * mm});
            skLineSegment(sketch, "E75.bottom", {"start": v(-255, 1903.24) * mm, "end": v(-195, 1903.24) * mm});
            skLineSegment(sketch, "E75.top", {"start": v(-255, 1863.24) * mm, "end": v(-195, 1863.24) * mm});
            skLineSegment(sketch, "E75.left", {"start": v(-255, 1903.24) * mm, "end": v(-255, 1863.24) * mm});
            skLineSegment(sketch, "E75.right", {"start": v(-195, 1903.24) * mm, "end": v(-195, 1863.24) * mm});
            skLineSegment(sketch, "E76.bottom", {"start": v(-430, 1903.24) * mm, "end": v(-370, 1903.24) * mm});
            skLineSegment(sketch, "E76.top", {"start": v(-430, 1863.24) * mm, "end": v(-370, 1863.24) * mm});
            skLineSegment(sketch, "E76.left", {"start": v(-430, 1903.24) * mm, "end": v(-430, 1863.24) * mm});
            skLineSegment(sketch, "E76.right", {"start": v(-370, 1903.24) * mm, "end": v(-370, 1863.24) * mm});
            skLineSegment(sketch, "E77.bottom", {"start": v(-605, 1903.24) * mm, "end": v(-545, 1903.24) * mm});
            skLineSegment(sketch, "E77.top", {"start": v(-605, 1863.24) * mm, "end": v(-545, 1863.24) * mm});
            skLineSegment(sketch, "E77.left", {"start": v(-605, 1903.24) * mm, "end": v(-605, 1863.24) * mm});
            skLineSegment(sketch, "E77.right", {"start": v(-545, 1903.24) * mm, "end": v(-545, 1863.24) * mm});
            skLineSegment(sketch, "E78.bottom", {"start": v(-780, 1903.24) * mm, "end": v(-720, 1903.24) * mm});
            skLineSegment(sketch, "E78.top", {"start": v(-780, 1863.24) * mm, "end": v(-720, 1863.24) * mm});
            skLineSegment(sketch, "E78.left", {"start": v(-780, 1903.24) * mm, "end": v(-780, 1863.24) * mm});
            skLineSegment(sketch, "E78.right", {"start": v(-720, 1903.24) * mm, "end": v(-720, 1863.24) * mm});
            skLineSegment(sketch, "E79.bottom", {"start": v(-955, 1903.24) * mm, "end": v(-895, 1903.24) * mm});
            skLineSegment(sketch, "E79.top", {"start": v(-955, 1863.24) * mm, "end": v(-895, 1863.24) * mm});
            skLineSegment(sketch, "E79.left", {"start": v(-955, 1903.24) * mm, "end": v(-955, 1863.24) * mm});
            skLineSegment(sketch, "E79.right", {"start": v(-895, 1903.24) * mm, "end": v(-895, 1863.24) * mm});
            skLineSegment(sketch, "E80.bottom", {"start": v(-1130, 1903.24) * mm, "end": v(-1070, 1903.24) * mm});
            skLineSegment(sketch, "E80.top", {"start": v(-1130, 1863.24) * mm, "end": v(-1070, 1863.24) * mm});
            skLineSegment(sketch, "E80.left", {"start": v(-1130, 1903.24) * mm, "end": v(-1130, 1863.24) * mm});
            skLineSegment(sketch, "E80.right", {"start": v(-1070, 1903.24) * mm, "end": v(-1070, 1863.24) * mm});
            skLineSegment(sketch, "E81.bottom", {"start": v(-1305, 1903.24) * mm, "end": v(-1245, 1903.24) * mm});
            skLineSegment(sketch, "E81.top", {"start": v(-1305, 1863.24) * mm, "end": v(-1245, 1863.24) * mm});
            skLineSegment(sketch, "E81.left", {"start": v(-1305, 1903.24) * mm, "end": v(-1305, 1863.24) * mm});
            skLineSegment(sketch, "E81.right", {"start": v(-1245, 1903.24) * mm, "end": v(-1245, 1863.24) * mm});
            skLineSegment(sketch, "E82.bottom", {"start": v(-1480, 1903.24) * mm, "end": v(-1420, 1903.24) * mm});
            skLineSegment(sketch, "E82.top", {"start": v(-1480, 1863.24) * mm, "end": v(-1420, 1863.24) * mm});
            skLineSegment(sketch, "E82.left", {"start": v(-1480, 1903.24) * mm, "end": v(-1480, 1863.24) * mm});
            skLineSegment(sketch, "E82.right", {"start": v(-1420, 1903.24) * mm, "end": v(-1420, 1863.24) * mm});
            skLineSegment(sketch, "E83.bottom", {"start": v(-1655, 1903.24) * mm, "end": v(-1595, 1903.24) * mm});
            skLineSegment(sketch, "E83.top", {"start": v(-1655, 1863.24) * mm, "end": v(-1595, 1863.24) * mm});
            skLineSegment(sketch, "E83.left", {"start": v(-1655, 1903.24) * mm, "end": v(-1655, 1863.24) * mm});
            skLineSegment(sketch, "E83.right", {"start": v(-1595, 1903.24) * mm, "end": v(-1595, 1863.24) * mm});
            skLineSegment(sketch, "E84.bottom", {"start": v(-1830, 1903.24) * mm, "end": v(-1770, 1903.24) * mm});
            skLineSegment(sketch, "E84.top", {"start": v(-1830, 1863.24) * mm, "end": v(-1770, 1863.24) * mm});
            skLineSegment(sketch, "E84.left", {"start": v(-1830, 1903.24) * mm, "end": v(-1830, 1863.24) * mm});
            skLineSegment(sketch, "E84.right", {"start": v(-1770, 1903.24) * mm, "end": v(-1770, 1863.24) * mm});
            skLineSegment(sketch, "E85.bottom", {"start": v(-2005, 1903.24) * mm, "end": v(-1945, 1903.24) * mm});
            skLineSegment(sketch, "E85.top", {"start": v(-2005, 1863.24) * mm, "end": v(-1945, 1863.24) * mm});
            skLineSegment(sketch, "E85.left", {"start": v(-2005, 1903.24) * mm, "end": v(-2005, 1863.24) * mm});
            skLineSegment(sketch, "E85.right", {"start": v(-1945, 1903.24) * mm, "end": v(-1945, 1863.24) * mm});
            skLineSegment(sketch, "E86.bottom", {"start": v(-2180, 1903.24) * mm, "end": v(-2120, 1903.24) * mm});
            skLineSegment(sketch, "E86.top", {"start": v(-2180, 1863.24) * mm, "end": v(-2120, 1863.24) * mm});
            skLineSegment(sketch, "E86.left", {"start": v(-2180, 1903.24) * mm, "end": v(-2180, 1863.24) * mm});
            skLineSegment(sketch, "E86.right", {"start": v(-2120, 1903.24) * mm, "end": v(-2120, 1863.24) * mm});
            skLineSegment(sketch, "E87.bottom", {"start": v(-2355, 1903.24) * mm, "end": v(-2295, 1903.24) * mm});
            skLineSegment(sketch, "E87.top", {"start": v(-2355, 1863.24) * mm, "end": v(-2295, 1863.24) * mm});
            skLineSegment(sketch, "E87.left", {"start": v(-2355, 1903.24) * mm, "end": v(-2355, 1863.24) * mm});
            skLineSegment(sketch, "E87.right", {"start": v(-2295, 1903.24) * mm, "end": v(-2295, 1863.24) * mm});
            skSolve(sketch);
        }
        {
            var Q0;
            Q0=makeQuery(id+"F17.imprint","IMPRINT",FACE,{"disambiguationData":[TD([[makeQuery(id+"F17.imprint","IMPRINT",EDGE,{"derivedFrom":sQuery(id+"F17.wireOp",EDGE,"E87.bottom")}),-1.0]])]});
            var Q1;
            Q1=makeQuery(id+"F17.imprint","IMPRINT",FACE,{"disambiguationData":[TD([[makeQuery(id+"F17.imprint","IMPRINT",EDGE,{"derivedFrom":sQuery(id+"F17.wireOp",EDGE,"E86.bottom")}),-1.0]])]});
            var Q2;
            Q2=makeQuery(id+"F17.imprint","IMPRINT",FACE,{"disambiguationData":[TD([[makeQuery(id+"F17.imprint","IMPRINT",EDGE,{"derivedFrom":sQuery(id+"F17.wireOp",EDGE,"E85.bottom")}),-1.0]])]});
            var Q3;
            Q3=makeQuery(id+"F17.imprint","IMPRINT",FACE,{"disambiguationData":[TD([[makeQuery(id+"F17.imprint","IMPRINT",EDGE,{"derivedFrom":sQuery(id+"F17.wireOp",EDGE,"E84.bottom")}),-1.0]])]});
            var Q4;
            Q4=makeQuery(id+"F17.imprint","IMPRINT",FACE,{"disambiguationData":[TD([[makeQuery(id+"F17.imprint","IMPRINT",EDGE,{"derivedFrom":sQuery(id+"F17.wireOp",EDGE,"E83.bottom")}),-1.0]])]});
            var Q5;
            Q5=makeQuery(id+"F17.imprint","IMPRINT",FACE,{"disambiguationData":[TD([[makeQuery(id+"F17.imprint","IMPRINT",EDGE,{"derivedFrom":sQuery(id+"F17.wireOp",EDGE,"E82.bottom")}),-1.0]])]});
            var Q6;
            Q6=makeQuery(id+"F17.imprint","IMPRINT",FACE,{"disambiguationData":[TD([[makeQuery(id+"F17.imprint","IMPRINT",EDGE,{"derivedFrom":sQuery(id+"F17.wireOp",EDGE,"E81.bottom")}),-1.0]])]});
            var Q7;
            Q7=makeQuery(id+"F17.imprint","IMPRINT",FACE,{"disambiguationData":[TD([[makeQuery(id+"F17.imprint","IMPRINT",EDGE,{"derivedFrom":sQuery(id+"F17.wireOp",EDGE,"E80.bottom")}),-1.0]])]});
            var Q8;
            Q8=makeQuery(id+"F17.imprint","IMPRINT",FACE,{"disambiguationData":[TD([[makeQuery(id+"F17.imprint","IMPRINT",EDGE,{"derivedFrom":sQuery(id+"F17.wireOp",EDGE,"E79.bottom")}),-1.0]])]});
            var Q9;
            Q9=makeQuery(id+"F17.imprint","IMPRINT",FACE,{"disambiguationData":[TD([[makeQuery(id+"F17.imprint","IMPRINT",EDGE,{"derivedFrom":sQuery(id+"F17.wireOp",EDGE,"E78.bottom")}),-1.0]])]});
            var Q10;
            Q10=makeQuery(id+"F17.imprint","IMPRINT",FACE,{"disambiguationData":[TD([[makeQuery(id+"F17.imprint","IMPRINT",EDGE,{"derivedFrom":sQuery(id+"F17.wireOp",EDGE,"E77.bottom")}),-1.0]])]});
            var Q11;
            Q11=makeQuery(id+"F17.imprint","IMPRINT",FACE,{"disambiguationData":[TD([[makeQuery(id+"F17.imprint","IMPRINT",EDGE,{"derivedFrom":sQuery(id+"F17.wireOp",EDGE,"E76.bottom")}),-1.0]])]});
            var Q12;
            Q12=makeQuery(id+"F17.imprint","IMPRINT",FACE,{"disambiguationData":[TD([[makeQuery(id+"F17.imprint","IMPRINT",EDGE,{"derivedFrom":sQuery(id+"F17.wireOp",EDGE,"E75.bottom")}),1.0]])]});
            extrude(context, id + "F18", {"entities" : qUnion([Q0, Q1, Q2, Q3, Q4, Q5, Q6, Q7, Q8, Q9, Q10, Q11, Q12]), "operationType" : NewBodyOperationType.ADD, "depth" : 390 * mm});
        }
        {
            var Q0;
            Q0=makeQuery(id+"F13.boolean.opBoolean","MERGE",FACE,{"derivedFrom":[makeQuery(id+"F7.opBoolean","MERGE",FACE,{"derivedFrom":[makeQuery(id+"F1.opExtrude","SWEPT_FACE",FACE,{"disambiguationData":[OSD([sQuery(id+"F0.wireOp",EDGE,"E1.left")])]}),makeQuery(id+"F5.opExtrude","SWEPT_FACE",FACE,{"disambiguationData":[OSD([sQuery(id+"F4.wireOp",EDGE,"E34.0")])]})]}),makeQuery(id+"F13.opExtrude","SWEPT_FACE",FACE,{"disambiguationData":[OSD([sQuery(id+"F12.wireOp",EDGE,"E45.left")])]})]});
            var sketch = newSketch(context, id + "F19", { "sketchPlane" : qUnion([Q0])});
            skLineSegment(sketch, "E88.bottom", {"start": v(-1913.24, 1210) * mm, "end": v(-1853.24, 1210) * mm});
            skLineSegment(sketch, "E88.top", {"start": v(-1913.24, 1180) * mm, "end": v(-1853.24, 1180) * mm});
            skLineSegment(sketch, "E88.left", {"start": v(-1913.24, 1210) * mm, "end": v(-1913.24, 1180) * mm});
            skLineSegment(sketch, "E88.right", {"start": v(-1853.24, 1210) * mm, "end": v(-1853.24, 1180) * mm});
            skSolve(sketch);
        }
        {
            var Q0;
            Q0=makeQuery(id+"F19.imprint","IMPRINT",FACE,{"disambiguationData":[TD([[makeQuery(id+"F19.imprint","IMPRINT",EDGE,{"derivedFrom":sQuery(id+"F19.wireOp",EDGE,"E88.bottom")}),-1.0]])]});
            extrude(context, id + "F20", {"entities" : qUnion([Q0]), "operationType" : NewBodyOperationType.ADD, "depth" : 2670 * mm});
        }
        {
            var Q0;
            Q0=makeQuery(id+"F20.opExtrude","SWEPT_FACE",FACE,{"disambiguationData":[OSD([sQuery(id+"F19.wireOp",EDGE,"E88.top")])]});
            var sketch = newSketch(context, id + "F21", { "sketchPlane" : qUnion([Q0])});
            skLineSegment(sketch, "E89.bottom", {"start": v(-2530, -1863.24) * mm, "end": v(-2470, -1863.24) * mm});
            skLineSegment(sketch, "E89.top", {"start": v(-2530, -1903.24) * mm, "end": v(-2470, -1903.24) * mm});
            skLineSegment(sketch, "E89.left", {"start": v(-2530, -1863.24) * mm, "end": v(-2530, -1903.24) * mm});
            skLineSegment(sketch, "E89.right", {"start": v(-2470, -1863.24) * mm, "end": v(-2470, -1903.24) * mm});
            skLineSegment(sketch, "E90.bottom", {"start": v(-2705, -1863.24) * mm, "end": v(-2645, -1863.24) * mm});
            skLineSegment(sketch, "E90.top", {"start": v(-2705, -1903.24) * mm, "end": v(-2645, -1903.24) * mm});
            skLineSegment(sketch, "E90.left", {"start": v(-2705, -1863.24) * mm, "end": v(-2705, -1903.24) * mm});
            skLineSegment(sketch, "E90.right", {"start": v(-2645, -1863.24) * mm, "end": v(-2645, -1903.24) * mm});
            skSolve(sketch);
        }
        {
            var Q0;
            Q0=makeQuery(id+"F21.imprint","IMPRINT",FACE,{"disambiguationData":[TD([[makeQuery(id+"F21.imprint","IMPRINT",EDGE,{"derivedFrom":sQuery(id+"F21.wireOp",EDGE,"E90.bottom")}),-1.0]])]});
            var Q1;
            Q1=makeQuery(id+"F21.imprint","IMPRINT",FACE,{"disambiguationData":[TD([[makeQuery(id+"F21.imprint","IMPRINT",EDGE,{"derivedFrom":sQuery(id+"F21.wireOp",EDGE,"E89.bottom")}),-1.0]])]});
            extrude(context, id + "F22", {"entities" : qUnion([Q0, Q1]), "operationType" : NewBodyOperationType.ADD, "depth" : 790 * mm});
        }
    });
